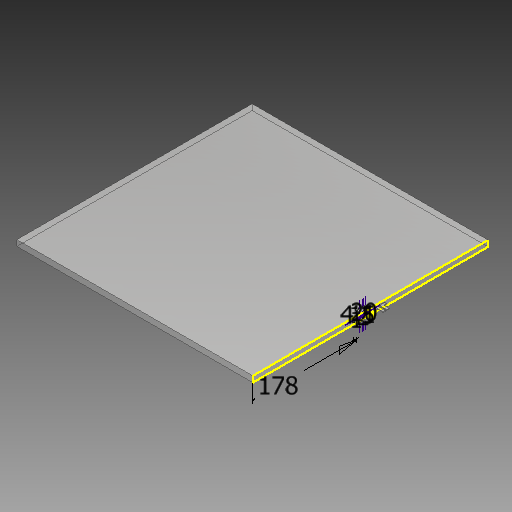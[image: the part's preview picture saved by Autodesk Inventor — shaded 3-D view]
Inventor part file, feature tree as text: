
AUTODESK INVENTOR PART (.ipt)
format: ipt  version: 2018.2 (Build 222227000, 227)  size: 149,504 bytes
history: native  units: mm
features: extrude x3, sketch x2, pattern_linear x1, projected_geometry x1
ambient origin geometry x8: Origin, YZ Plane, XZ Plane, XY Plane, X Axis, Y Axis, Z Axis, Center Point
bodies: Volumenkörper1 (feature_tree)
feature tree (7):
  extrude  "Extrusion1"  Depth=400.0mm
  sketch  "Skizze2"  dims[d2=10.0mm d3=0.0mm d4=20.0mm d5=1.0mm d6=11.0mm d7=2.0mm d8=4.5mm d10=178.0mm d11=4.0mm d12=0.0mm d15=13.0mm d16=0.0mm d17=20.0mm d19=27.0mm]
  extrude  "Extrusion2"  Depth=20.0mm
  extrude  "Extrusion4"  Depth=1.0mm
  pattern_linear  "Rechteckige Anordnung1"  Spacing1=11.0mm  [1 undecoded]
  sketch  "Skizze1"  dims[d0=400.0mm d1=400.0mm]
  projected_geometry  "Projizierte Kontur1"
note: 1 required parameter value undecoded (feature->parameter linkage not recoverable at this tier; creation-order binding heuristic only, values carry confidence <= 0.55)
